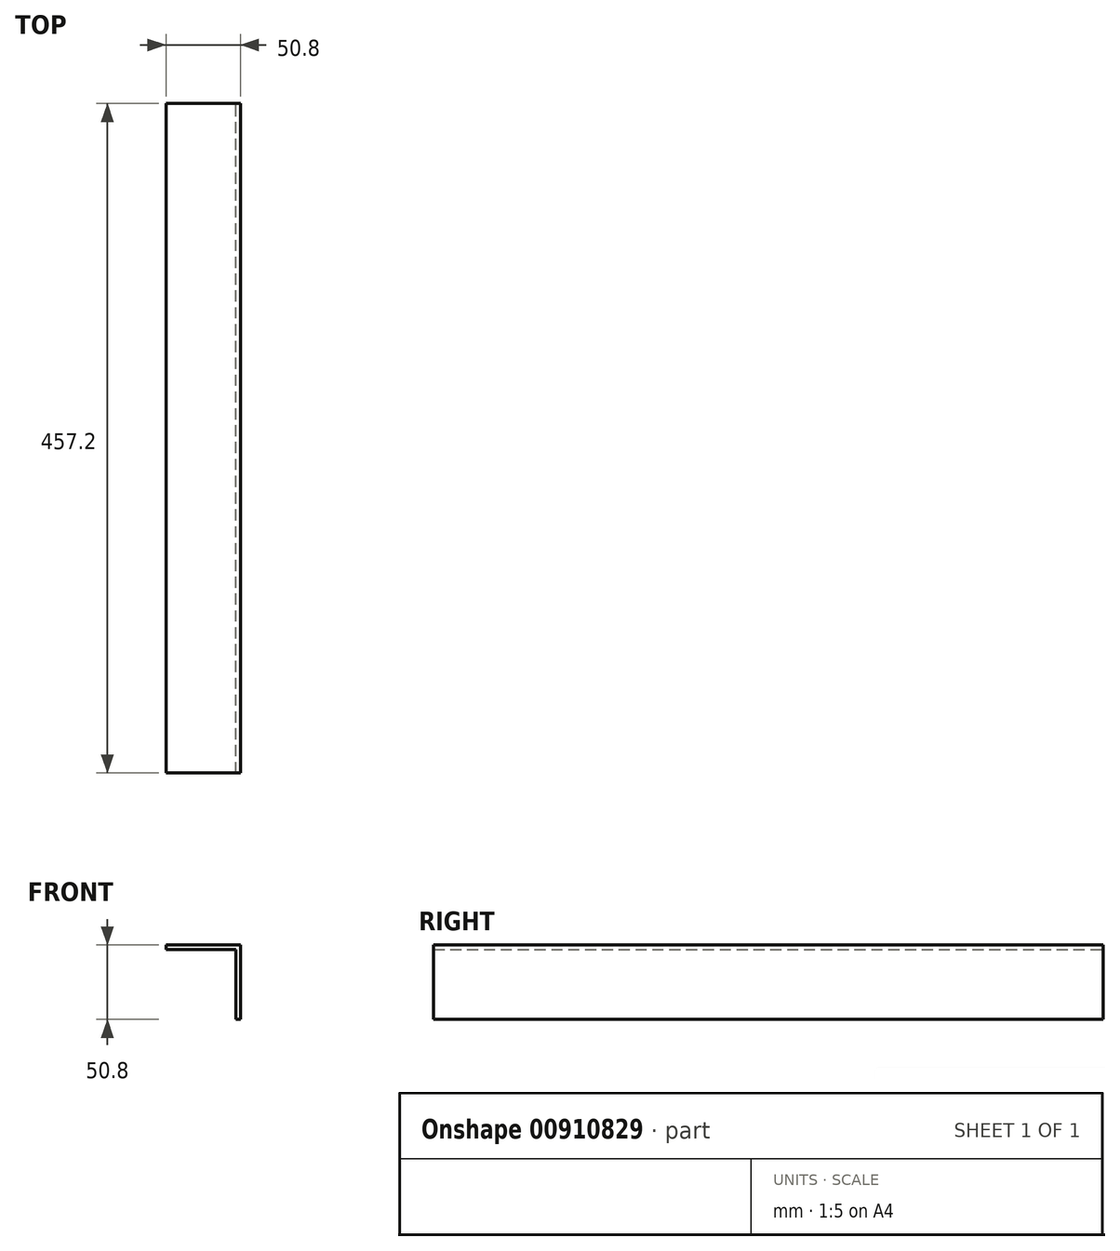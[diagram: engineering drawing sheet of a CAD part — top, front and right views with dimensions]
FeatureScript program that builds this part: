
annotation { "Feature Type Name" : "Feature", "Feature Type Description" : "" }
export const myFeature = defineFeature(function(context is Context, id is Id, definition is map)
    precondition{}
    {
        {
            var Q0;
            Q0=qCreatedBy(makeId("Front.planeOp"),FACE);
            var sketch = newSketch(context, id + "F0", { "sketchPlane" : qUnion([Q0])});
            skLineSegment(sketch, "E0", {"start": v(0, 0) * mm, "end": v(50.8, 0) * mm});
            skLineSegment(sketch, "E1", {"start": v(50.8, 0) * mm, "end": v(50.8, -50.8) * mm});
            skLineSegment(sketch, "E2.0", {"start": v(0, -3.18) * mm, "end": v(47.63, -3.18) * mm});
            skLineSegment(sketch, "E3.0", {"start": v(47.63, -3.18) * mm, "end": v(47.63, -50.8) * mm});
            skLineSegment(sketch, "E4", {"start": v(0, 0) * mm, "end": v(0, -3.18) * mm});
            skLineSegment(sketch, "E5", {"start": v(50.8, -50.8) * mm, "end": v(47.63, -50.8) * mm});
            skSolve(sketch);
        }
        {
            var Q0;
            Q0 = qSketchRegion(id + "F0", true);
            extrude(context, id + "F1", {"entities" : qUnion([Q0]), "depth" : 457.2 * mm, "offsetDistance" : 25.4 * mm});
        }
    });
